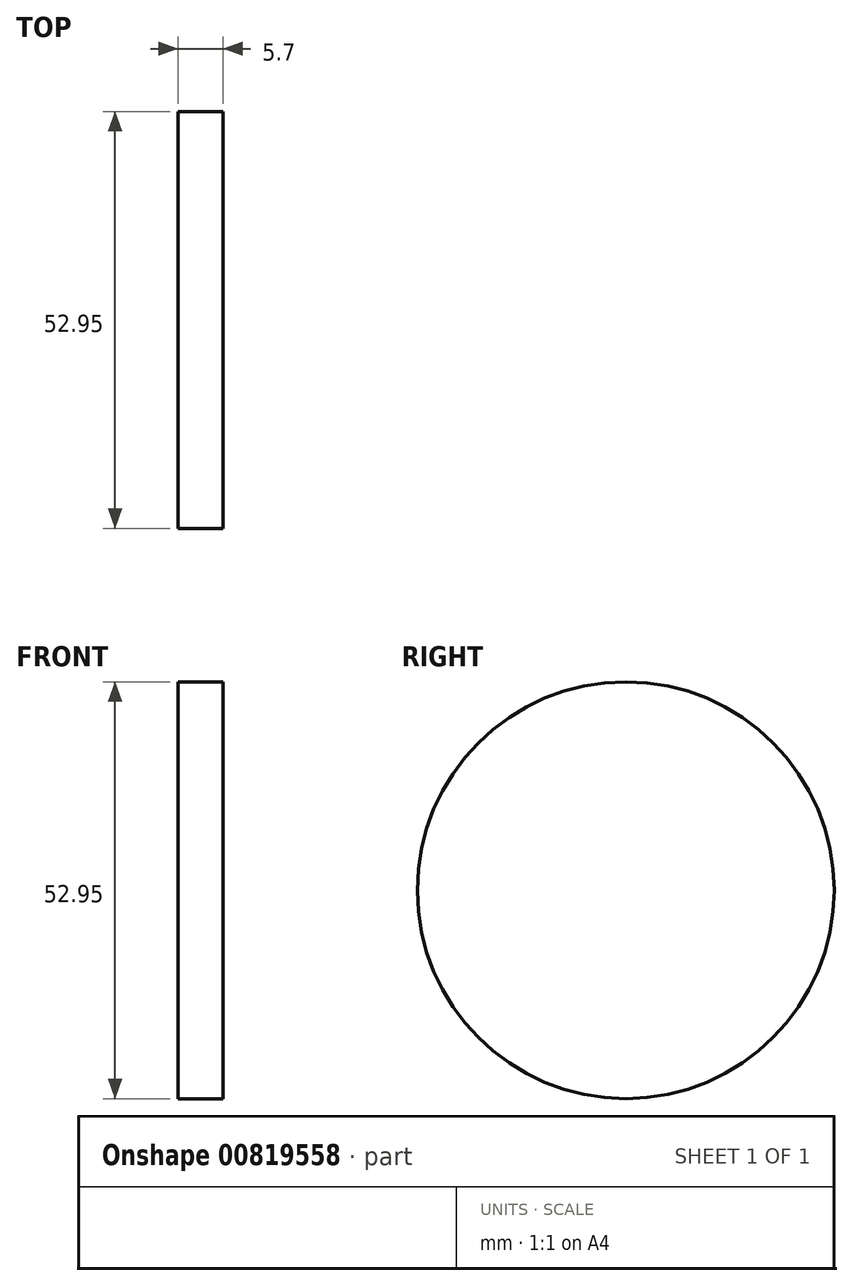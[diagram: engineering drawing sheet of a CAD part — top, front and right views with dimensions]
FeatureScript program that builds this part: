
annotation { "Feature Type Name" : "Feature", "Feature Type Description" : "" }
export const myFeature = defineFeature(function(context is Context, id is Id, definition is map)
    precondition{}
    {
        {
            var Q0;
            Q0=qCreatedBy(makeId("Right.planeOp"),FACE);
            var sketch = newSketch(context, id + "F0", { "sketchPlane" : qUnion([Q0])});
            skCircle(sketch, "E0", {"center": v(-40.77, 28.32) * mm, "radius": 26.47 * mm});
            skCircle(sketch, "E1", {"center": v(-40.77, 28.32) * mm, "radius": 22.17 * mm});
            skSolve(sketch);
        }
        {
            var Q0;
            Q0 = qSketchRegion(id + "F0", true);
            var Q1;
            Q1=makeQuery(id+"F0.imprint","IMPRINT",FACE,{"disambiguationData":[TD([[makeQuery(id+"F0.imprint","IMPRINT",EDGE,{"derivedFrom":sQuery(id+"F0.wireOp",EDGE,"E1")}),1.0]])]});
            extrude(context, id + "F1", {"entities" : qUnion([Q0, Q1]), "depth" : 5.7 * mm, "offsetDistance" : 25 * mm});
        }
    });
